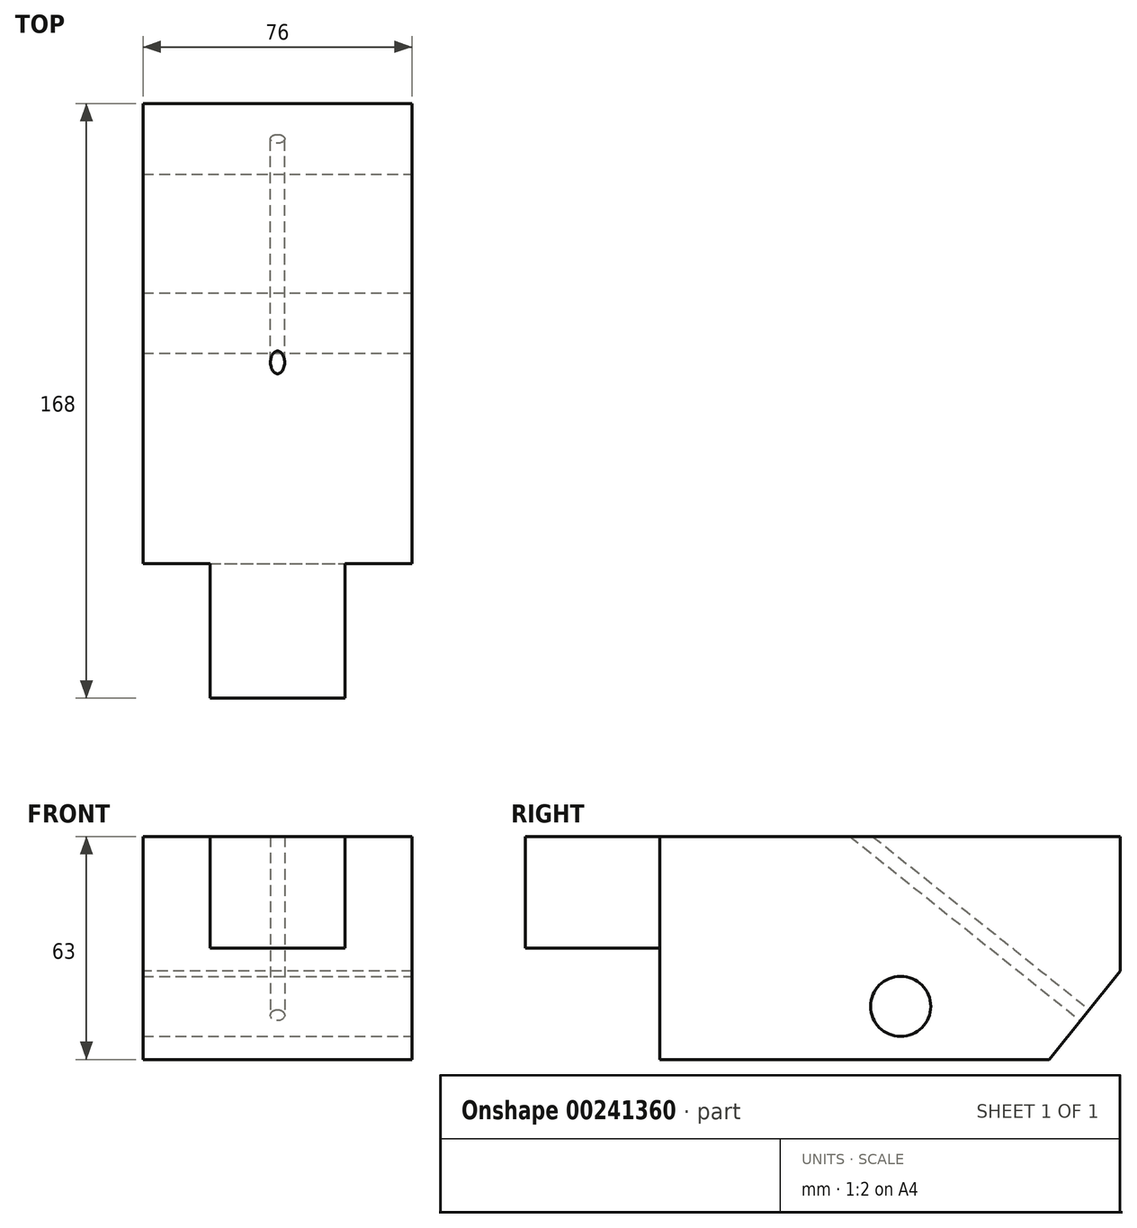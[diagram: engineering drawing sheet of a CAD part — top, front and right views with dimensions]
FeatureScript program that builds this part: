
annotation { "Feature Type Name" : "Feature", "Feature Type Description" : "" }
export const myFeature = defineFeature(function(context is Context, id is Id, definition is map)
    precondition{}
    {
        {
            var Q0;
            Q0=qCreatedBy(makeId("Top.planeOp"),FACE);
            var sketch = newSketch(context, id + "F0", { "sketchPlane" : qUnion([Q0])});
            skLineSegment(sketch, "E0.bottom", {"start": v(-38, 65) * mm, "end": v(38, 65) * mm});
            skLineSegment(sketch, "E0.top", {"start": v(-38, -65) * mm, "end": v(38, -65) * mm});
            skLineSegment(sketch, "E0.left", {"start": v(-38, 65) * mm, "end": v(-38, -65) * mm});
            skLineSegment(sketch, "E0.right", {"start": v(38, 65) * mm, "end": v(38, -65) * mm});
            skPoint(sketch, "E0.middle", {"position": v(0, 0) * mm});
            skSolve(sketch);
        }
        {
            var Q0;
            Q0 = qSketchRegion(id + "F0", true);
            extrude(context, id + "F1", {"entities" : qUnion([Q0]), "depth" : 63 * mm});
        }
        {
            var Q0;
            Q0=makeQuery(id+"F1.opExtrude","CAP_EDGE",EDGE,{"disambiguationData":[OSD([sQuery(id+"F0.wireOp",EDGE,"E0.bottom")])],"isStart":true});
            chamfer(context, id + "F2", {"entities" : qUnion([Q0]), "chamferType" : ChamferType.TWO_OFFSETS, "width1" : 20 * mm, "oppositeDirection" : false, "width2" : 25 * mm, "tangentPropagation" : true});
        }
        {
            var Q0;
            Q0=makeQuery(id+"F2.opChamfer","BLEND_FACE",FACE,{"disambiguationData":[OSD([sQuery(id+"F0.wireOp",EDGE,"E0.bottom")])]});
            var sketch = newSketch(context, id + "F3", { "sketchPlane" : qUnion([Q0])});
            skCircle(sketch, "E1", {"center": v(0, 44.12) * mm, "radius": 2 * mm});
            skPoint(sketch, "E1.centerSnap0", {"position": v(38, 44.12) * mm});
            skSolve(sketch);
        }
        {
            var Q0;
            Q0 = qSketchRegion(id + "F3", true);
            extrude(context, id + "F4", {"entities" : qUnion([Q0]), "operationType" : NewBodyOperationType.REMOVE, "endBound" : BoundingType.THROUGH_ALL, "oppositeDirection" : true, "depth" : 25 * mm});
        }
        {
            var Q0;
            Q0=makeQuery(id+"F1.opExtrude","SWEPT_FACE",FACE,{"disambiguationData":[OSD([sQuery(id+"F0.wireOp",EDGE,"E0.right")])]});
            var sketch = newSketch(context, id + "F5", { "sketchPlane" : qUnion([Q0])});
            skCircle(sketch, "E2", {"center": v(3, 15) * mm, "radius": 8.5 * mm});
            skSolve(sketch);
        }
        {
            var Q0;
            Q0 = qSketchRegion(id + "F5", true);
            extrude(context, id + "F6", {"entities" : qUnion([Q0]), "operationType" : NewBodyOperationType.REMOVE, "endBound" : BoundingType.THROUGH_ALL, "oppositeDirection" : true, "depth" : 25 * mm});
        }
        {
            var Q0;
            Q0=makeQuery(id+"F1.opExtrude","SWEPT_FACE",FACE,{"disambiguationData":[OSD([sQuery(id+"F0.wireOp",EDGE,"E0.top")])]});
            var sketch = newSketch(context, id + "F7", { "sketchPlane" : qUnion([Q0])});
            skLineSegment(sketch, "E3.bottom", {"start": v(-19, 63) * mm, "end": v(19, 63) * mm});
            skLineSegment(sketch, "E3.top", {"start": v(-19, 0) * mm, "end": v(19, 0) * mm});
            skLineSegment(sketch, "E3.left", {"start": v(-19, 63) * mm, "end": v(-19, 0) * mm});
            skLineSegment(sketch, "E3.right", {"start": v(19, 63) * mm, "end": v(19, 0) * mm});
            skPoint(sketch, "E3.middle", {"position": v(0, 31.5) * mm});
            skPoint(sketch, "E3.middle.positionSnap0", {"position": v(-38, 31.5) * mm});
            skPoint(sketch, "E3.centerSnap0", {"position": v(-38, 31.5) * mm});
            skLineSegment(sketch, "E4", {"start": v(-19, 31.5) * mm, "end": v(19, 31.5) * mm});
            skSolve(sketch);
        }
        {
            var Q0;
            {var subQ0=sQuery(id+"F7.wireOp",EDGE,"E3.bottom");Q0=makeQuery(id+"F7.imprint","IMPRINT",FACE,{"disambiguationData":[TD([[makeQuery(id+"F7.imprint","IMPRINT",EDGE,{"derivedFrom":subQ0}),-1.0]])]});}
            extrude(context, id + "F8", {"entities" : qUnion([Q0]), "operationType" : NewBodyOperationType.ADD, "depth" : 38 * mm});
        }
    });
